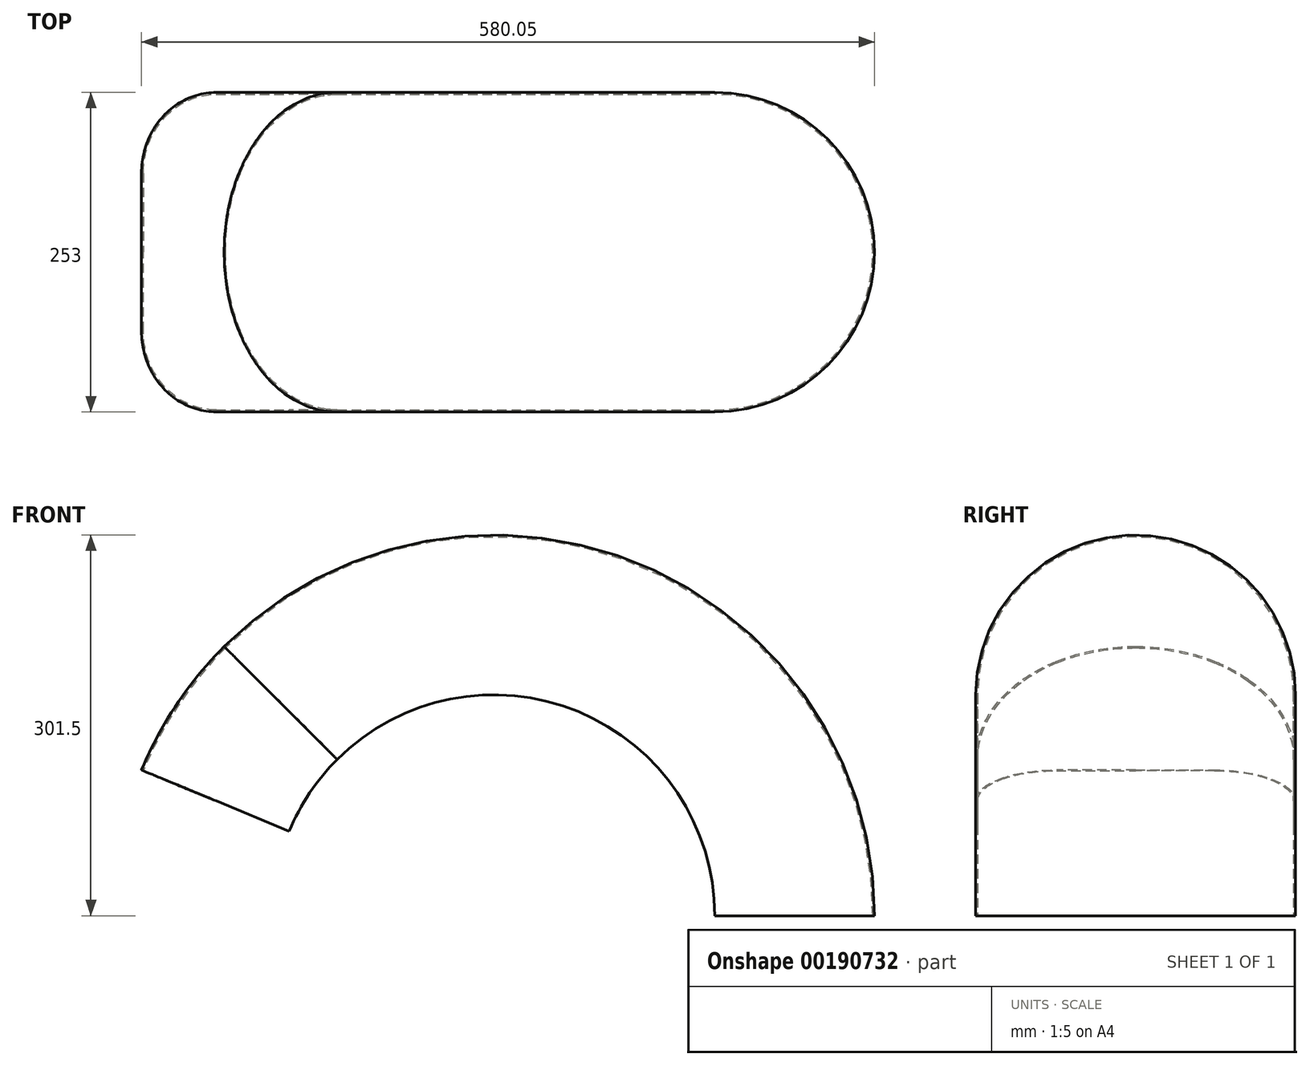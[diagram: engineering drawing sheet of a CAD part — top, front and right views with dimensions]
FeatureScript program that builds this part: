
annotation { "Feature Type Name" : "Feature", "Feature Type Description" : "" }
export const myFeature = defineFeature(function(context is Context, id is Id, definition is map)
    precondition{}
    {
        {
            var Q0;
            Q0=qCreatedBy(makeId("Top.planeOp"),FACE);
            var sketch = newSketch(context, id + "F0", { "sketchPlane" : qUnion([Q0])});
            skArc(sketch, "E0", {"start": v(175, -125) * mm, "mid": v(300, 0) * mm, "end": v(175, 125) * mm});
            skArc(sketch, "E1", {"start": v(175, -126.5) * mm, "mid": v(301.5, 0) * mm, "end": v(175, 126.5) * mm});
            skLineSegment(sketch, "E2", {"start": v(175, 126.5) * mm, "end": v(175, 125) * mm});
            skLineSegment(sketch, "E3", {"start": v(175, -126.5) * mm, "end": v(175, -125) * mm});
            skLineSegment(sketch, "E4", {"start": v(0, -67.72) * mm, "end": v(0, 0) * mm, "construction": true});
            skSolve(sketch);
        }
        {
            var Q0;
            Q0 = qSketchRegion(id + "F0", true);
            var Q1;
            Q1=sQuery(id+"F0.wireOp",EDGE,"E4");
            revolve(context, id + "F1", {"entities" : qUnion([Q0]), "axis" : qUnion([Q1]), "revolveType" : RevolveType.ONE_DIRECTION, "oppositeDirection" : true, "angle" : 135 * degree});
        }
        {
            var Q0;
            Q0=qCreatedBy(makeId("Front.planeOp"),FACE);
            var sketch = newSketch(context, id + "F2", { "sketchPlane" : qUnion([Q0])});
            skLineSegment(sketch, "E5", {"start": v(0, 0) * mm, "end": v(-345.99, 143.31) * mm, "construction": true});
            skSolve(sketch);
        }
        {
            var Q0;
            Q0=qCreatedBy(makeId("Top.planeOp"),FACE);
            var Q1;
            Q1=sQuery(id+"F2.wireOp",EDGE,"E5");
            cPlane(context, id + "F3", {"entities" : qUnion([Q0, Q1]), "cplaneType" : CPlaneType.LINE_ANGLE, "offset" : 25 * mm, "angle" : 0 * degree, "width" : 150 * mm, "height" : 150 * mm});
        }
        {
            var Q0;
            Q0=qCreatedBy(id+"F3.planeOp",FACE);
            var sketch = newSketch(context, id + "F4", { "sketchPlane" : qUnion([Q0])});
            skLineSegment(sketch, "E6", {"start": v(-300, -62.5) * mm, "end": v(-300, 0) * mm});
            skArc(sketch, "E7", {"start": v(-300, -62.5) * mm, "mid": v(-295.24, -86.42) * mm, "end": v(-281.7, -106.7) * mm});
            skLineSegment(sketch, "E8", {"start": v(-237.5, -125) * mm, "end": v(-175, -125) * mm});
            skLineSegment(sketch, "E9", {"start": v(-301.5, 0) * mm, "end": v(-301.5, -62.5) * mm});
            skLineSegment(sketch, "E10", {"start": v(-175, -126.5) * mm, "end": v(-237.5, -126.5) * mm});
            skArc(sketch, "E11", {"start": v(-301.5, -62.5) * mm, "mid": v(-296.63, -87) * mm, "end": v(-282.75, -107.75) * mm});
            skLineSegment(sketch, "E12", {"start": v(-175, -126.5) * mm, "end": v(-175, -125) * mm});
            skLineSegment(sketch, "E13.MirrorCS", {"start": v(-175, 126.5) * mm, "end": v(-175, 125) * mm});
            skLineSegment(sketch, "E14.MirrorCS", {"start": v(-300, 62.5) * mm, "end": v(-300, 0) * mm});
            skLineSegment(sketch, "E15.MirrorCS", {"start": v(-237.5, 125) * mm, "end": v(-175, 125) * mm});
            skArc(sketch, "E16.MirrorCS", {"start": v(-301.5, 62.5) * mm, "mid": v(-296.63, 87) * mm, "end": v(-282.75, 107.75) * mm});
            skLineSegment(sketch, "E17.MirrorCS", {"start": v(-175, 126.5) * mm, "end": v(-237.5, 126.5) * mm});
            skLineSegment(sketch, "E18.MirrorCS", {"start": v(-301.5, 0) * mm, "end": v(-301.5, 62.5) * mm});
            skArc(sketch, "E19.MirrorCS", {"start": v(-300, 62.5) * mm, "mid": v(-295.24, 86.42) * mm, "end": v(-281.7, 106.7) * mm});
            skPoint(sketch, "E20", {"position": v(-282.75, 107.75) * mm});
            skPoint(sketch, "E21", {"position": v(-281.7, 106.7) * mm});
            skPoint(sketch, "E22", {"position": v(-282.75, -107.75) * mm});
            skPoint(sketch, "E23", {"position": v(-281.7, -106.7) * mm});
            skArc(sketch, "E24", {"start": v(-281.7, -106.7) * mm, "mid": v(-261.42, -120.24) * mm, "end": v(-237.5, -125) * mm});
            skArc(sketch, "E25", {"start": v(-282.75, -107.75) * mm, "mid": v(-262, -121.63) * mm, "end": v(-237.5, -126.5) * mm});
            skArc(sketch, "E26", {"start": v(-281.7, 106.7) * mm, "mid": v(-261.42, 120.24) * mm, "end": v(-237.5, 125) * mm});
            skArc(sketch, "E27", {"start": v(-282.75, 107.75) * mm, "mid": v(-262, 121.63) * mm, "end": v(-237.5, 126.5) * mm});
            skPoint(sketch, "E28", {"position": v(0, -62.5) * mm});
            skPoint(sketch, "E29", {"position": v(0, 62.5) * mm});
            skSolve(sketch);
        }
        {
            var Q0;
            Q0=qCreatedBy(makeId("Front.planeOp"),FACE);
            var sketch = newSketch(context, id + "F5", { "sketchPlane" : qUnion([Q0])});
            skPoint(sketch, "E30.0", {"position": v(-213.2, 213.2) * mm});
            skPoint(sketch, "E31.0", {"position": v(-278.55, 115.38) * mm});
            skArc(sketch, "E32", {"start": v(-213.2, 213.2) * mm, "mid": v(-250.69, 167.5) * mm, "end": v(-278.55, 115.38) * mm});
            skPoint(sketch, "E33", {"position": v(-250.69, 167.5) * mm});
            skArc(sketch, "E34", {"start": v(-212.13, 212.13) * mm, "mid": v(-249.44, 166.67) * mm, "end": v(-277.16, 114.8) * mm});
            skPoint(sketch, "E35", {"position": v(-249.44, 166.67) * mm});
            skSolve(sketch);
        }
        {
            var Q0;
            Q0=qCreatedBy(makeId("Front.planeOp"),FACE);
            cPlane(context, id + "F6", {"entities" : qUnion([Q0]), "cplaneType" : CPlaneType.OFFSET, "offset" : 126.5 * mm, "width" : 150 * mm, "height" : 150 * mm});
        }
        {
            var Q0;
            Q0=qCreatedBy(id+"F6.planeOp",FACE);
            var sketch = newSketch(context, id + "F7", { "sketchPlane" : qUnion([Q0])});
            skArc(sketch, "E36", {"start": v(-123.74, 123.74) * mm, "mid": v(-145.5, 97.22) * mm, "end": v(-161.68, 66.97) * mm});
            skSolve(sketch);
        }
        {
            var Q0;
            Q0=qCreatedBy(makeId("Front.planeOp"),FACE);
            cPlane(context, id + "F8", {"entities" : qUnion([Q0]), "cplaneType" : CPlaneType.OFFSET, "offset" : 126.5 * mm, "oppositeDirection" : true, "width" : 150 * mm, "height" : 150 * mm});
        }
        {
            var Q0;
            Q0=qCreatedBy(id+"F8.planeOp",FACE);
            var sketch = newSketch(context, id + "F9", { "sketchPlane" : qUnion([Q0])});
            skArc(sketch, "E37", {"start": v(-123.74, 123.74) * mm, "mid": v(-145.5, 97.22) * mm, "end": v(-161.68, 66.97) * mm});
            skSolve(sketch);
        }
        {
            var Q0;
            Q0=qCreatedBy(makeId("Front.planeOp"),FACE);
            cPlane(context, id + "F10", {"entities" : qUnion([Q0]), "cplaneType" : CPlaneType.OFFSET, "offset" : 125 * mm, "width" : 150 * mm, "height" : 150 * mm});
        }
        {
            var Q0;
            Q0=qCreatedBy(id+"F10.planeOp",FACE);
            var sketch = newSketch(context, id + "F11", { "sketchPlane" : qUnion([Q0])});
            skPoint(sketch, "E38.0", {"position": v(0, 0) * mm});
            skArc(sketch, "E39", {"start": v(-161.68, 66.97) * mm, "mid": v(-145.5, 97.22) * mm, "end": v(-123.74, 123.74) * mm});
            skSolve(sketch);
        }
        {
            var Q0;
            Q0=qCreatedBy(makeId("Front.planeOp"),FACE);
            cPlane(context, id + "F12", {"entities" : qUnion([Q0]), "cplaneType" : CPlaneType.OFFSET, "offset" : 125 * mm, "oppositeDirection" : true, "width" : 150 * mm, "height" : 150 * mm});
        }
        {
            var Q0;
            Q0=qCreatedBy(id+"F12.planeOp",FACE);
            var sketch = newSketch(context, id + "F13", { "sketchPlane" : qUnion([Q0])});
            skPoint(sketch, "E40.0", {"position": v(0, 0) * mm});
            skArc(sketch, "E41", {"start": v(-123.74, 123.74) * mm, "mid": v(-145.5, 97.22) * mm, "end": v(-161.68, 66.97) * mm});
            skSolve(sketch);
        }
        {
            var Q0;
            Q0=qCreatedBy(makeId("Front.planeOp"),FACE);
            var Q1;
            Q1=sQuery(id+"F4.wireOp",VERTEX,"E29");
            cPlane(context, id + "F14", {"entities" : qUnion([Q0, Q1]), "cplaneType" : CPlaneType.PLANE_POINT, "offset" : 25 * mm, "width" : 150 * mm, "height" : 150 * mm});
        }
        {
            var Q0;
            Q0=qCreatedBy(makeId("Front.planeOp"),FACE);
            var Q1;
            Q1=sQuery(id+"F4.wireOp",VERTEX,"E28");
            cPlane(context, id + "F15", {"entities" : qUnion([Q0, Q1]), "cplaneType" : CPlaneType.PLANE_POINT, "offset" : 25 * mm, "width" : 150 * mm, "height" : 150 * mm});
        }
        {
            var Q0;
            Q0=makeQuery(id+"F1.opRevolve","CAP_FACE",FACE,{"disambiguationData":[OSD([sQuery(id+"F0.wireOp",EDGE,"E0"),sQuery(id+"F0.wireOp",EDGE,"E1"),sQuery(id+"F0.wireOp",EDGE,"E2"),sQuery(id+"F0.wireOp",EDGE,"E3")])],"isStart":false});
            var sketch = newSketch(context, id + "F16", { "sketchPlane" : qUnion([Q0])});
            skLineSegment(sketch, "E42", {"start": v(0, 301.5) * mm, "end": v(0, 175) * mm, "construction": true});
            skLineSegment(sketch, "E43", {"start": v(0, 175) * mm, "end": v(89.45, 264.45) * mm, "construction": true});
            skLineSegment(sketch, "E44", {"start": v(0, 175) * mm, "end": v(-89.45, 264.45) * mm, "construction": true});
            skPoint(sketch, "E45", {"position": v(89.45, 264.45) * mm});
            skPoint(sketch, "E46", {"position": v(-89.45, 264.45) * mm});
            skPoint(sketch, "E47", {"position": v(62.5, 284.98) * mm});
            skPoint(sketch, "E48", {"position": v(62.5, 283.25) * mm});
            skPoint(sketch, "E49", {"position": v(-62.5, 284.98) * mm});
            skPoint(sketch, "E50", {"position": v(-62.5, 283.25) * mm});
            skArc(sketch, "E51.0", {"start": v(125, 175) * mm, "mid": v(124.88, 180.45) * mm, "end": v(124.52, 185.9) * mm});
            skArc(sketch, "E52.0", {"start": v(126.5, 175) * mm, "mid": v(126.38, 180.52) * mm, "end": v(126.02, 186.03) * mm});
            skArc(sketch, "E53", {"start": v(-88.39, 263.39) * mm, "mid": v(-113.29, 227.83) * mm, "end": v(-124.52, 185.9) * mm});
            skArc(sketch, "E54", {"start": v(-89.45, 264.45) * mm, "mid": v(-114.65, 228.46) * mm, "end": v(-126.02, 186.03) * mm});
            skArc(sketch, "E55", {"start": v(-62.5, 284.98) * mm, "mid": v(-76.67, 275.62) * mm, "end": v(-89.45, 264.45) * mm});
            skArc(sketch, "E56", {"start": v(-62.5, 283.25) * mm, "mid": v(-76.1, 274.17) * mm, "end": v(-88.39, 263.39) * mm});
            skArc(sketch, "E57", {"start": v(0, 301.5) * mm, "mid": v(-32.32, 297.3) * mm, "end": v(-62.5, 284.98) * mm});
            skArc(sketch, "E58", {"start": v(0, 300) * mm, "mid": v(-32.35, 295.74) * mm, "end": v(-62.5, 283.25) * mm});
            skArc(sketch, "E59", {"start": v(62.5, 284.98) * mm, "mid": v(32.32, 297.3) * mm, "end": v(0, 301.5) * mm});
            skArc(sketch, "E60", {"start": v(62.5, 283.25) * mm, "mid": v(32.35, 295.74) * mm, "end": v(0, 300) * mm});
            skArc(sketch, "E61", {"start": v(89.45, 264.45) * mm, "mid": v(76.67, 275.62) * mm, "end": v(62.5, 284.98) * mm});
            skArc(sketch, "E62", {"start": v(88.39, 263.39) * mm, "mid": v(76.1, 274.17) * mm, "end": v(62.5, 283.25) * mm});
            skLineSegment(sketch, "E63", {"start": v(0, 175) * mm, "end": v(-126.02, 186.03) * mm, "construction": true});
            skLineSegment(sketch, "E64", {"start": v(0, 175) * mm, "end": v(-116.5, 175) * mm, "construction": true});
            skLineSegment(sketch, "E65.MirrorCS", {"start": v(0, 175) * mm, "end": v(126.02, 186.03) * mm, "construction": true});
            skArc(sketch, "E66", {"start": v(-126.02, 186.03) * mm, "mid": v(-126.38, 180.52) * mm, "end": v(-126.5, 175) * mm});
            skArc(sketch, "E67", {"start": v(-124.52, 185.9) * mm, "mid": v(-124.88, 180.45) * mm, "end": v(-125, 175) * mm});
            skArc(sketch, "E68", {"start": v(124.52, 185.9) * mm, "mid": v(113.29, 227.83) * mm, "end": v(88.39, 263.39) * mm});
            skArc(sketch, "E69", {"start": v(126.02, 186.03) * mm, "mid": v(114.65, 228.46) * mm, "end": v(89.45, 264.45) * mm});
            skLineSegment(sketch, "E70.0", {"start": v(126.5, 175) * mm, "end": v(125, 175) * mm});
            skLineSegment(sketch, "E71.0", {"start": v(-126.5, 175) * mm, "end": v(-125, 175) * mm});
            skSolve(sketch);
        }
        {
            var Q0;
            Q0=sQuery(id+"F4.wireOp",VERTEX,"E22");
            var Q1;
            Q1=sQuery(id+"F4.wireOp",VERTEX,"E7.center");
            var Q2;
            Q2=sQuery(id+"F16.wireOp",VERTEX,"E46");
            cPlane(context, id + "F17", {"entities" : qUnion([Q0, Q1, Q2]), "cplaneType" : CPlaneType.THREE_POINT, "offset" : 25 * mm, "width" : 150 * mm, "height" : 150 * mm});
        }
        {
            var Q0;
            Q0=qCreatedBy(id+"F17.planeOp",FACE);
            var sketch = newSketch(context, id + "F18", { "sketchPlane" : qUnion([Q0])});
            skLineSegment(sketch, "E72", {"start": v(234.22, 147.26) * mm, "end": v(141.97, 206.8) * mm});
            skSolve(sketch);
        }
        {
            var Q0;
            Q0=sQuery(id+"F16.wireOp",VERTEX,"E45");
            var Q1;
            Q1=sQuery(id+"F4.wireOp",VERTEX,"E20");
            var Q2;
            Q2=sQuery(id+"F4.wireOp",VERTEX,"E16.MirrorCS.center");
            cPlane(context, id + "F19", {"entities" : qUnion([Q0, Q1, Q2]), "cplaneType" : CPlaneType.THREE_POINT, "offset" : 25 * mm, "width" : 150 * mm, "height" : 150 * mm});
        }
        {
            var Q0;
            Q0=qCreatedBy(id+"F19.planeOp",FACE);
            var sketch = newSketch(context, id + "F20", { "sketchPlane" : qUnion([Q0])});
            skLineSegment(sketch, "E73", {"start": v(234.22, 147.26) * mm, "end": v(141.97, 206.8) * mm});
            skSolve(sketch);
        }
        {
            var Q0;
            Q0=qCreatedBy(id+"F14.planeOp",FACE);
            var sketch = newSketch(context, id + "F21", { "sketchPlane" : qUnion([Q0])});
            skLineSegment(sketch, "E74", {"start": v(-278.55, 115.38) * mm, "end": v(-201.51, 201.51) * mm});
            skLineSegment(sketch, "E75", {"start": v(-277.16, 114.8) * mm, "end": v(-200.3, 200.3) * mm});
            skSolve(sketch);
        }
        {
            var Q0;
            Q0=qCreatedBy(id+"F15.planeOp",FACE);
            var sketch = newSketch(context, id + "F22", { "sketchPlane" : qUnion([Q0])});
            skLineSegment(sketch, "E76", {"start": v(-278.55, 115.38) * mm, "end": v(-201.51, 201.51) * mm});
            skLineSegment(sketch, "E77", {"start": v(-200.3, 200.3) * mm, "end": v(-277.16, 114.8) * mm});
            skSolve(sketch);
        }
        {
            var Q1;
            Q1 = qSketchRegion(id + "F16", true);
            var Q2;
            Q2 = qSketchRegion(id + "F4", true);
            var Q3;
            Q3=sQuery(id+"F11.wireOp",EDGE,"E39");
            var Q4;
            Q4=sQuery(id+"F7.wireOp",EDGE,"E36");
            var Q5;
            Q5=sQuery(id+"F20.wireOp",EDGE,"E73");
            var Q6;
            Q6=sQuery(id+"F21.wireOp",EDGE,"E74");
            var Q7;
            Q7=sQuery(id+"F21.wireOp",EDGE,"E75");
            var Q8;
            Q8=sQuery(id+"F5.wireOp",EDGE,"E32");
            var Q9;
            Q9=sQuery(id+"F5.wireOp",EDGE,"E34");
            var Q10;
            Q10=sQuery(id+"F22.wireOp",EDGE,"E76");
            var Q11;
            Q11=sQuery(id+"F22.wireOp",EDGE,"E77");
            var Q12;
            Q12=sQuery(id+"F18.wireOp",EDGE,"E72");
            var Q13;
            Q13=sQuery(id+"F13.wireOp",EDGE,"E41");
            var Q14;
            Q14=sQuery(id+"F9.wireOp",EDGE,"E37");
            loft(context, id + "F23", {"operationType" : NewBodyOperationType.ADD, "addGuides" : true, "sheetProfilesArray" : [{ "sheetProfileEntities" : qUnion([Q1]) }, { "sheetProfileEntities" : qUnion([Q2]) }], "guidesArray" : [{ "guideEntities" : qUnion([Q3]), "guideDerivativeType" : LoftGuideDerivativeType.DEFAULT, "guideDerivativeMagnitude" : 1 }, { "guideEntities" : qUnion([Q4]), "guideDerivativeType" : LoftGuideDerivativeType.DEFAULT, "guideDerivativeMagnitude" : 1 }, { "guideEntities" : qUnion([Q5]), "guideDerivativeType" : LoftGuideDerivativeType.DEFAULT, "guideDerivativeMagnitude" : 1 }, { "guideEntities" : qUnion([Q6]), "guideDerivativeType" : LoftGuideDerivativeType.DEFAULT, "guideDerivativeMagnitude" : 1 }, { "guideEntities" : qUnion([Q7]), "guideDerivativeType" : LoftGuideDerivativeType.DEFAULT, "guideDerivativeMagnitude" : 1 }, { "guideEntities" : qUnion([Q8]), "guideDerivativeType" : LoftGuideDerivativeType.DEFAULT, "guideDerivativeMagnitude" : 1 }, { "guideEntities" : qUnion([Q9]), "guideDerivativeType" : LoftGuideDerivativeType.DEFAULT, "guideDerivativeMagnitude" : 1 }, { "guideEntities" : qUnion([Q10]), "guideDerivativeType" : LoftGuideDerivativeType.DEFAULT, "guideDerivativeMagnitude" : 1 }, { "guideEntities" : qUnion([Q11]), "guideDerivativeType" : LoftGuideDerivativeType.DEFAULT, "guideDerivativeMagnitude" : 1 }, { "guideEntities" : qUnion([Q12]), "guideDerivativeType" : LoftGuideDerivativeType.DEFAULT, "guideDerivativeMagnitude" : 1 }, { "guideEntities" : qUnion([Q13]), "guideDerivativeType" : LoftGuideDerivativeType.DEFAULT, "guideDerivativeMagnitude" : 1 }, { "guideEntities" : qUnion([Q14]), "guideDerivativeType" : LoftGuideDerivativeType.DEFAULT, "guideDerivativeMagnitude" : 1 }]});
        }
    });
